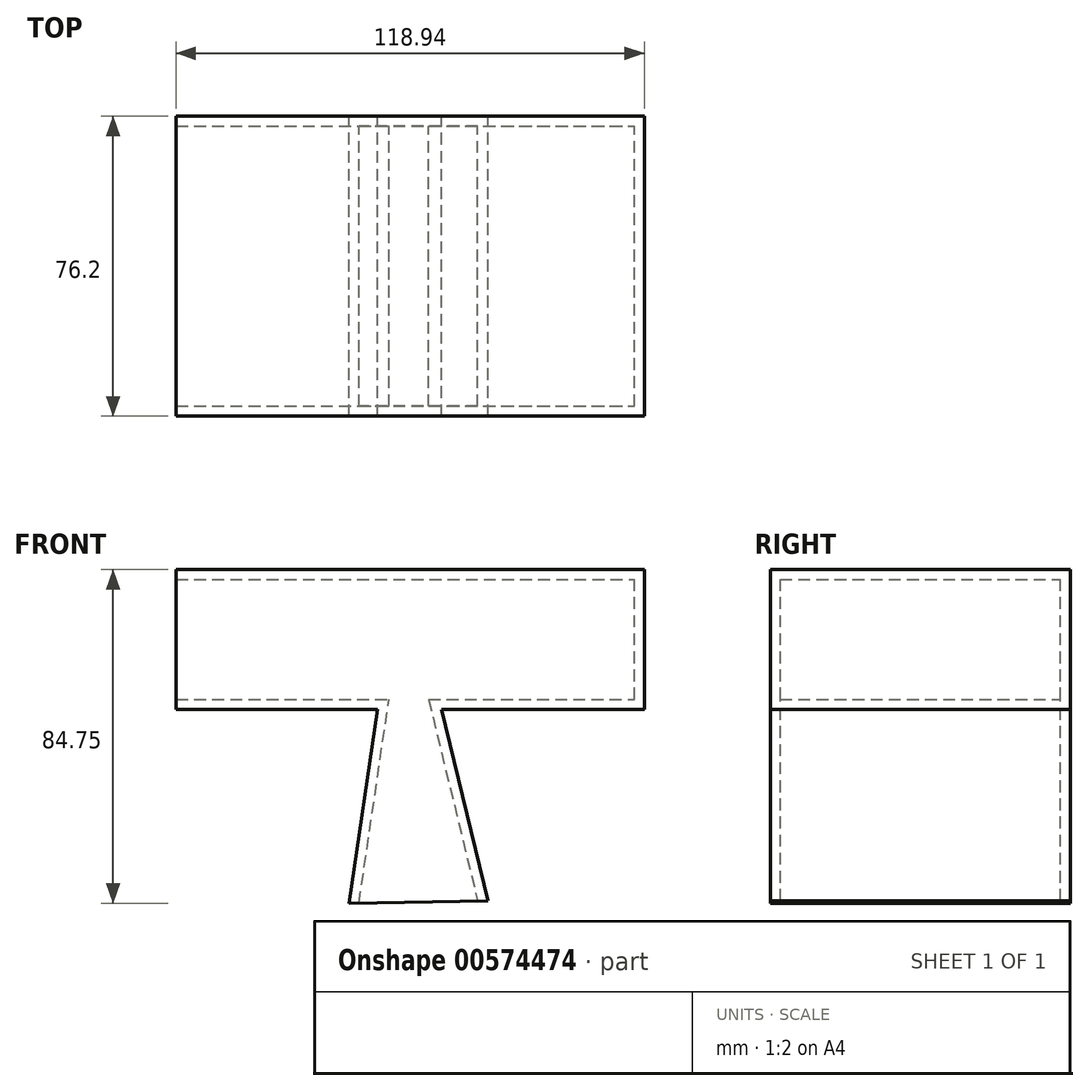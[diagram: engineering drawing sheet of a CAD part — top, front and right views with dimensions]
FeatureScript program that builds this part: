
annotation { "Feature Type Name" : "Feature", "Feature Type Description" : "" }
export const myFeature = defineFeature(function(context is Context, id is Id, definition is map)
    precondition{}
    {
        {
            var Q0;
            Q0=qCreatedBy(makeId("Front.planeOp"),FACE);
            var sketch = newSketch(context, id + "F0", { "sketchPlane" : qUnion([Q0])});
            skLineSegment(sketch, "E0.bottom", {"start": v(-59.47, -17.76) * mm, "end": v(59.47, -17.76) * mm});
            skLineSegment(sketch, "E0.top", {"start": v(-59.47, 17.76) * mm, "end": v(59.47, 17.76) * mm});
            skLineSegment(sketch, "E0.left", {"start": v(-59.47, -17.76) * mm, "end": v(-59.47, 17.76) * mm});
            skLineSegment(sketch, "E0.right", {"start": v(59.47, -17.76) * mm, "end": v(59.47, 17.76) * mm});
            skPoint(sketch, "E0.middle", {"position": v(0, 0) * mm});
            skLineSegment(sketch, "E1", {"start": v(7.91, -17.76) * mm, "end": v(19.76, -66.33) * mm});
            skLineSegment(sketch, "E2", {"start": v(19.76, -66.33) * mm, "end": v(-15.57, -67) * mm});
            skLineSegment(sketch, "E3", {"start": v(-15.57, -67) * mm, "end": v(-8.33, -17.76) * mm});
            skSolve(sketch);
        }
        {
            var Q0;
            Q0 = qSketchRegion(id + "F0", true);
            var Q1;
            Q1=makeQuery(id+"F0.imprint","IMPRINT",FACE,{"disambiguationData":[TD([[makeQuery(id+"F0.imprint","IMPRINT",EDGE,{"derivedFrom":sQuery(id+"F0.wireOp",EDGE,"E0.top")}),-1.0]])]});
            extrude(context, id + "F1", {"entities" : qUnion([Q0, Q1]), "depth" : 76.2 * mm, "offsetDistance" : 25.4 * mm});
        }
        {
            var Q0;
            Q0=makeQuery(id+"F1.opExtrude","SWEPT_FACE",FACE,{"disambiguationData":[OSD([sQuery(id+"F0.wireOp",EDGE,"E2")])]});
            var Q1;
            Q1=makeQuery(id+"F1.opExtrude","SWEPT_FACE",FACE,{"disambiguationData":[OSD([sQuery(id+"F0.wireOp",EDGE,"E0.left")])]});
            shell(context, id + "F2", {"entities" : qUnion([Q0, Q1]), "thickness" : 2.54 * mm});
        }
    });
